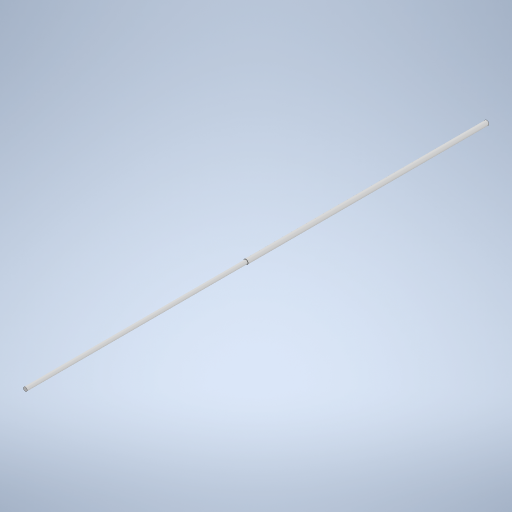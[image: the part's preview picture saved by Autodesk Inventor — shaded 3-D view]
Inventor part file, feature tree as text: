
AUTODESK INVENTOR PART (.ipt)
format: ipt  version: 2023.1 (Build 271208000, 208)  size: 239,616 bytes
history: native  units: mm
features: extrude x2, other x1, sketch x1
ambient origin geometry x8: Origin, YZ Plane, XZ Plane, XY Plane, X Axis, Y Axis, Z Axis, Center Point
bodies: Body1 (feature_tree)
feature tree (4):
  other  "솔리드1"
  sketch  "스케치1"
  extrude  "돌출1"  Depth=22.5mm
  extrude  "돌출2"  Depth=18.5mm
